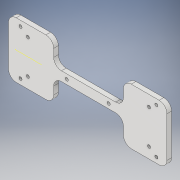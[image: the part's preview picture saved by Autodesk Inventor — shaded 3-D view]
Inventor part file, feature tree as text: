
AUTODESK INVENTOR PART (.ipt)
format: ipt  version: 2019 (Build 230136000, 136)  size: 213,504 bytes
history: native  units: mm
features: extrude x5, sketch x5, plane x3, mirror x1, fillet x1
ambient origin geometry x8: Origin, YZ Plane, XZ Plane, XY Plane, X Axis, Y Axis, Z Axis, Center Point
bodies: Solid1 (feature_tree)
feature tree (15):
  extrude  "Extrusion1"  Depth=72.0mm
  extrude  "Extrusion4"  Depth=6.0mm TaperAngle=0.0deg
  plane  "Work Plane1"
  plane  "Work Plane2"
  extrude  "Extrusion5"  Depth=4.0mm
  plane  "Work Plane3"
  mirror  "Mirror1"
  fillet  "Fillet1"  Radius=4.0mm
  extrude  "Extrusion6"  [1 undecoded]
  extrude  "Extrusion7"  Depth=6.0mm
  sketch  "Sketch1"  dims[d0=204.0mm d1=72.0mm]
  sketch  "Sketch4"  dims[d2=10.0mm d3=6.0mm d4=0.0mm]
  sketch  "Sketch5"  dims[d6=4.0mm d17=4.0mm d19=4.0mm]
  sketch  "Sketch7"  dims[d21=6.0mm d22=0.0mm d23=-100.0mm]
  sketch  "Sketch8"  dims[d24=-36.0mm d25=31.0mm d26=30.0mm d27=31.0mm d28=30.0mm d29=35.0mm d30=35.0mm d34=6.0mm d35=0.0mm d36=-36.0mm d37=10.0mm d38=14.0mm d39=14.0mm d40=25.0mm d41=25.0mm d43=156.0mm d44=156.0mm d45=79.0mm d46=15.0mm d47=15.0mm d48=10.0mm d49=4.0mm d50=4.0mm d54=7.0mm d55=6.0mm d56=0.0mm d57=42.694526mm d58=42.694526mm d59=42.5mm d60=42.5mm d61=102.0mm d62=4.0mm d63=4.0mm d64=75.0mm d65=75.0mm d66=6.0mm d67=0.0mm]
note: 1 required parameter value undecoded (feature->parameter linkage not recoverable at this tier; creation-order binding heuristic only, values carry confidence <= 0.55)
